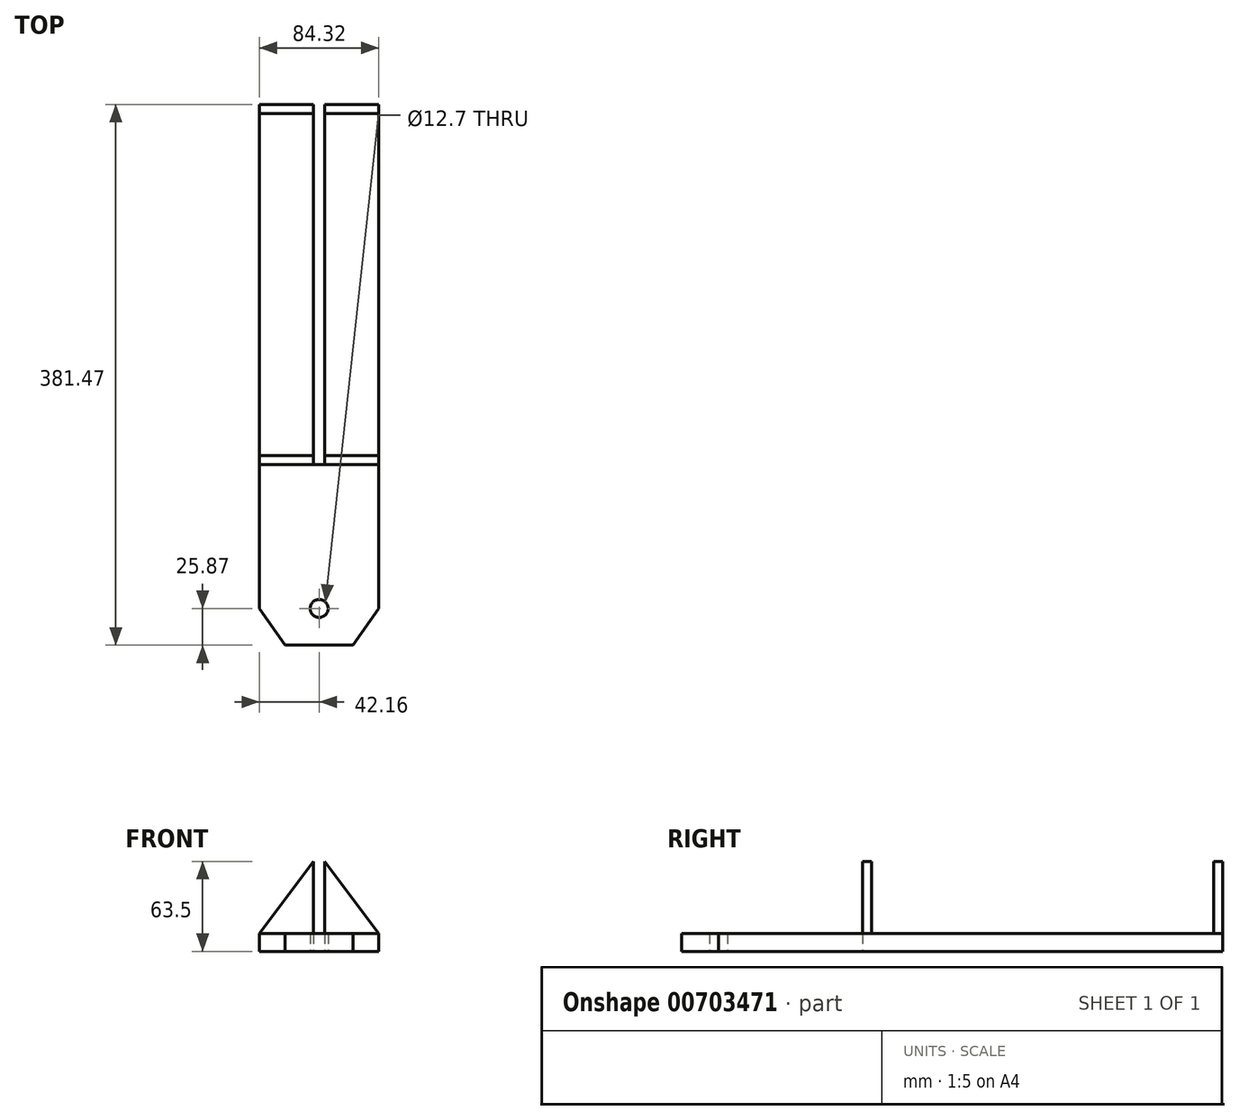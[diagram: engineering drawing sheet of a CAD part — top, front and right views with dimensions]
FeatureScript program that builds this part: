
annotation { "Feature Type Name" : "Feature", "Feature Type Description" : "" }
export const myFeature = defineFeature(function(context is Context, id is Id, definition is map)
    precondition{}
    {
        {
            var Q0;
            Q0=qCreatedBy(makeId("Top.planeOp"),FACE);
            var sketch = newSketch(context, id + "F0", { "sketchPlane" : qUnion([Q0])});
            skLineSegment(sketch, "E0.top", {"start": v(4.06, -127) * mm, "end": v(-4.06, -127) * mm});
            skLineSegment(sketch, "E0.left", {"start": v(4.06, 127) * mm, "end": v(4.06, -127) * mm});
            skLineSegment(sketch, "E0.right", {"start": v(-4.06, 127) * mm, "end": v(-4.06, -127) * mm});
            skPoint(sketch, "E0.middle", {"position": v(0, 0) * mm});
            skLineSegment(sketch, "E1.bottom", {"start": v(4.06, 127) * mm, "end": v(42.16, 127) * mm});
            skLineSegment(sketch, "E1.right", {"start": v(42.16, 127) * mm, "end": v(42.16, -127) * mm});
            skLineSegment(sketch, "E2.bottom", {"start": v(-4.06, 127) * mm, "end": v(-42.16, 127) * mm});
            skLineSegment(sketch, "E2.right", {"start": v(-42.16, 127) * mm, "end": v(-42.16, -127) * mm});
            skLineSegment(sketch, "E3.bottom", {"start": v(-4.06, -127) * mm, "end": v(4.06, -127) * mm});
            skLineSegment(sketch, "E3.top", {"start": v(-42.16, -228.6) * mm, "end": v(-6.35, -228.6) * mm});
            skLineSegment(sketch, "E3.left", {"start": v(-42.16, -127) * mm, "end": v(-42.16, -228.6) * mm});
            skLineSegment(sketch, "E3.right", {"start": v(42.16, -127) * mm, "end": v(42.16, -228.6) * mm});
            skLineSegment(sketch, "E4", {"start": v(-42.16, -228.6) * mm, "end": v(-24.05, -254.47) * mm});
            skLineSegment(sketch, "E5", {"start": v(42.16, -228.6) * mm, "end": v(24.05, -254.47) * mm});
            skLineSegment(sketch, "E6", {"start": v(-24.05, -254.47) * mm, "end": v(24.05, -254.47) * mm});
            skCircle(sketch, "E7", {"center": v(0, -228.6) * mm, "radius": 6.35 * mm});
            skLineSegment(sketch, "E8.trimOffspring", {"start": v(6.35, -228.6) * mm, "end": v(42.16, -228.6) * mm});
            skSolve(sketch);
        }
        {
            var Q0;
            Q0 = qSketchRegion(id + "F0", true);
            extrude(context, id + "F1", {"entities" : qUnion([Q0]), "depth" : 12.7 * mm, "offsetDistance" : 25.4 * mm});
        }
        {
            var Q0;
            Q0=makeQuery(id+"F1.opExtrude","CAP_FACE",FACE,{"disambiguationData":[OSD([sQuery(id+"F0.wireOp",EDGE,"E1.bottom"),sQuery(id+"F0.wireOp",EDGE,"E0.left"),sQuery(id+"F0.wireOp",EDGE,"E1.right"),sQuery(id+"F0.wireOp",EDGE,"E2.bottom"),sQuery(id+"F0.wireOp",EDGE,"E0.right"),sQuery(id+"F0.wireOp",EDGE,"E2.right"),sQuery(id+"F0.wireOp",EDGE,"E3.bottom"),sQuery(id+"F0.wireOp",EDGE,"E3.left"),sQuery(id+"F0.wireOp",EDGE,"E3.right"),sQuery(id+"F0.wireOp",EDGE,"E4"),sQuery(id+"F0.wireOp",EDGE,"E5"),sQuery(id+"F0.wireOp",EDGE,"E6"),sQuery(id+"F0.wireOp",EDGE,"E7")])],"isStart":false});
            var sketch = newSketch(context, id + "F2", { "sketchPlane" : qUnion([Q0])});
            skLineSegment(sketch, "E9", {"start": v(-4.06, -127) * mm, "end": v(-42.16, -127) * mm});
            skLineSegment(sketch, "E10", {"start": v(-42.16, -127) * mm, "end": v(-42.16, -120.65) * mm});
            skLineSegment(sketch, "E11", {"start": v(-42.16, -120.65) * mm, "end": v(-4.06, -120.65) * mm});
            skLineSegment(sketch, "E12", {"start": v(-4.06, -120.65) * mm, "end": v(-4.06, -127) * mm});
            skSolve(sketch);
        }
        {
            var Q0;
            Q0 = qSketchRegion(id + "F2", true);
            extrude(context, id + "F3", {"entities" : qUnion([Q0]), "operationType" : NewBodyOperationType.ADD, "depth" : 50.8 * mm, "offsetDistance" : 25.4 * mm});
        }
        {
            var Q0;
            Q0=makeQuery(id+"F3.opExtrude","SWEPT_FACE",FACE,{"disambiguationData":[OSD([sQuery(id+"F2.wireOp",EDGE,"E9")])]});
            var sketch = newSketch(context, id + "F4", { "sketchPlane" : qUnion([Q0])});
            skLineSegment(sketch, "E13", {"start": v(-4.06, 63.5) * mm, "end": v(-42.16, 12.7) * mm});
            skLineSegment(sketch, "E14", {"start": v(-42.16, 12.7) * mm, "end": v(-42.16, 63.5) * mm});
            skLineSegment(sketch, "E15", {"start": v(-4.06, 63.5) * mm, "end": v(-42.16, 63.5) * mm});
            skSolve(sketch);
        }
        {
            var Q0;
            Q0 = qSketchRegion(id + "F4", true);
            extrude(context, id + "F5", {"entities" : qUnion([Q0]), "operationType" : NewBodyOperationType.REMOVE, "oppositeDirection" : true, "depth" : 25.4 * mm, "offsetDistance" : 25.4 * mm});
        }
        {
            var Q0;
            Q0=makeQuery(id+"F1.opExtrude","SWEPT_BODY",BODY,{"disambiguationData":[OSD([sQuery(id+"F0.wireOp",EDGE,"E1.bottom"),sQuery(id+"F0.wireOp",EDGE,"E0.left"),sQuery(id+"F0.wireOp",EDGE,"E1.right"),sQuery(id+"F0.wireOp",EDGE,"E2.bottom"),sQuery(id+"F0.wireOp",EDGE,"E0.right"),sQuery(id+"F0.wireOp",EDGE,"E2.right"),sQuery(id+"F0.wireOp",EDGE,"E3.bottom"),sQuery(id+"F0.wireOp",EDGE,"E3.left"),sQuery(id+"F0.wireOp",EDGE,"E3.right"),sQuery(id+"F0.wireOp",EDGE,"E4"),sQuery(id+"F0.wireOp",EDGE,"E5"),sQuery(id+"F0.wireOp",EDGE,"E6"),sQuery(id+"F0.wireOp",EDGE,"E7")])]});
            var Q1;
            Q1=qCreatedBy(makeId("Right.planeOp"),FACE);
            mirror(context, id + "F6", {"operationType" : NewBodyOperationType.ADD, "entities" : qUnion([Q0]), "mirrorPlane" : qUnion([Q1])});
        }
        {
            var Q0;
            Q0=makeQuery(id+"F1.opExtrude","SWEPT_BODY",BODY,{"disambiguationData":[OSD([sQuery(id+"F0.wireOp",EDGE,"E1.bottom"),sQuery(id+"F0.wireOp",EDGE,"E0.left"),sQuery(id+"F0.wireOp",EDGE,"E1.right"),sQuery(id+"F0.wireOp",EDGE,"E2.bottom"),sQuery(id+"F0.wireOp",EDGE,"E0.right"),sQuery(id+"F0.wireOp",EDGE,"E2.right"),sQuery(id+"F0.wireOp",EDGE,"E3.bottom"),sQuery(id+"F0.wireOp",EDGE,"E3.left"),sQuery(id+"F0.wireOp",EDGE,"E3.right"),sQuery(id+"F0.wireOp",EDGE,"E4"),sQuery(id+"F0.wireOp",EDGE,"E5"),sQuery(id+"F0.wireOp",EDGE,"E6"),sQuery(id+"F0.wireOp",EDGE,"E7")])]});
            var Q1;
            Q1=qCreatedBy(makeId("Front.planeOp"),FACE);
            mirror(context, id + "F7", {"operationType" : NewBodyOperationType.ADD, "entities" : qUnion([Q0]), "mirrorPlane" : qUnion([Q1])});
        }
        {
            var Q0;
            {var subQ1=sQuery(id+"F0.wireOp",EDGE,"E3.right");var subQ2=sQuery(id+"F0.wireOp",EDGE,"E1.right");var subQ4=sQuery(id+"F0.wireOp",EDGE,"E7");var subQ6=sQuery(id+"F0.wireOp",EDGE,"E6");var subQ8=sQuery(id+"F0.wireOp",EDGE,"E5");var subQ10=sQuery(id+"F0.wireOp",EDGE,"E4");var subQ13=sQuery(id+"F0.wireOp",EDGE,"E3.bottom");var subQ15=sQuery(id+"F0.wireOp",EDGE,"E0.left");var subQ18=sQuery(id+"F0.wireOp",EDGE,"E0.right");var subQ19=makeQuery(id+"F1.opExtrude","SWEPT_FACE",FACE,{"disambiguationData":[OSD([subQ18])]});var subQ20=sQuery(id+"F0.wireOp",EDGE,"E3.left");var subQ21=sQuery(id+"F0.wireOp",EDGE,"E2.right");var subQ24=sQuery(id+"F0.wireOp",EDGE,"E1.bottom");Q0=makeQuery(id+"F7.opPattern","COPY",FACE,{"derivedFrom":makeQuery(id+"F6.boolean.opBoolean","SPLIT",FACE,{"disambiguationData":[TD([subQ19])],"derivedFrom":makeQuery(id+"F3.boolean.opBoolean","SPLIT",FACE,{"disambiguationData":[TD([makeQuery(id+"F1.opExtrude","SWEPT_FACE",FACE,{"disambiguationData":[OSD([subQ24])]})])],"derivedFrom":makeQuery(id+"F1.opExtrude","CAP_FACE",FACE,{"disambiguationData":[OSD([subQ24,subQ15,subQ2,sQuery(id+"F0.wireOp",EDGE,"E2.bottom"),subQ18,subQ21,subQ13,subQ20,subQ1,subQ10,subQ8,subQ6,subQ4])],"isStart":false})})}),"instanceName":"1"});}
            var sketch = newSketch(context, id + "F8", { "sketchPlane" : qUnion([Q0])});
            skLineSegment(sketch, "E16.bottom", {"start": v(-42.16, 127) * mm, "end": v(88.37, 127) * mm});
            skLineSegment(sketch, "E16.top", {"start": v(-42.16, 294.27) * mm, "end": v(88.37, 294.27) * mm});
            skLineSegment(sketch, "E16.left", {"start": v(-42.16, 127) * mm, "end": v(-42.16, 294.27) * mm});
            skLineSegment(sketch, "E16.right", {"start": v(88.37, 127) * mm, "end": v(88.37, 294.27) * mm});
            skSolve(sketch);
        }
        {
            var Q0;
            Q0 = qSketchRegion(id + "F8", true);
            extrude(context, id + "F9", {"entities" : qUnion([Q0]), "operationType" : NewBodyOperationType.REMOVE, "oppositeDirection" : true, "depth" : 25.4 * mm, "offsetDistance" : 25.4 * mm});
        }
    });
